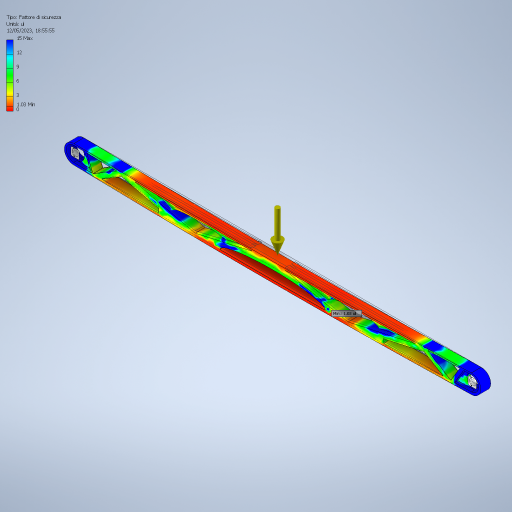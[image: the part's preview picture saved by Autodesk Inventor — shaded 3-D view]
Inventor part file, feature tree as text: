
AUTODESK INVENTOR PART (.ipt)
format: ipt  version: 2023 (Build 270158000, 158)  size: 517,120 bytes
history: native  units: mm
features: extrude x14, sketch x1
ambient origin geometry x8: Origin, YZ Plane, XZ Plane, XY Plane, X Axis, Y Axis, Z Axis, Center Point
bodies: Body1 (feature_tree)
feature tree (15):
  sketch  "Schizzo1"
  extrude  "Estrusione9"  Depth=30.0mm
  extrude  "Estrusione10"  Depth=30.0mm
  extrude  "Estrusione11"  Depth=800.0mm
  extrude  "Estrusione12"  Depth=3.0mm
  extrude  "Estrusione14"  Depth=20.0mm TaperAngle=0.0deg
  extrude  "Estrusione15"  Depth=4.0mm TaperAngle=0.0deg
  extrude  "Estrusione16"  Depth=20.0mm TaperAngle=0.0deg
  extrude  "Estrusione17"  Depth=7.0mm TaperAngle=0.0deg
  extrude  "Estrusione18"  Depth=20.0mm TaperAngle=0.0deg
  extrude  "Estrusione20"  Depth=7.0mm TaperAngle=0.0deg
  extrude  "Estrusione21"  Depth=20.0mm TaperAngle=0.0deg
  extrude  "Estrusione22"  Depth=20.0mm TaperAngle=0.0deg
  extrude  "Estrusione24"  Depth=4.0mm TaperAngle=0.0deg
  extrude  "Estrusione25"  Depth=20.0mm TaperAngle=0.0deg
